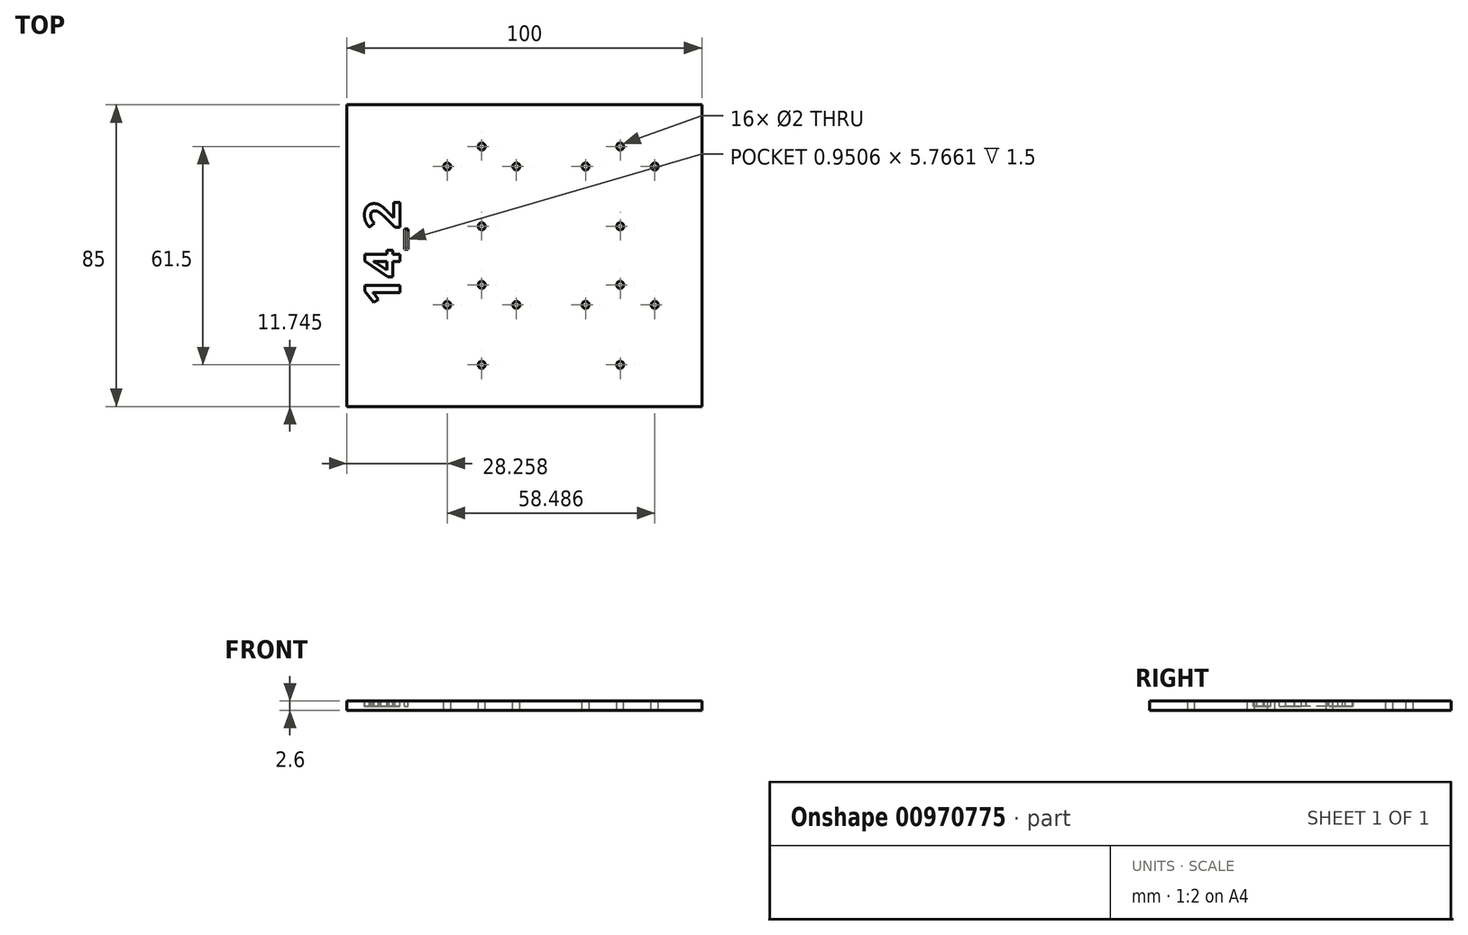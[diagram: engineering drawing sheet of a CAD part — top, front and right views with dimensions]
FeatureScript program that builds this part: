
annotation { "Feature Type Name" : "Feature", "Feature Type Description" : "" }
export const myFeature = defineFeature(function(context is Context, id is Id, definition is map)
    precondition{}
    {
        {
            var Q0;
            Q0=qCreatedBy(makeId("Top.planeOp"),FACE);
            var sketch = newSketch(context, id + "F0", { "sketchPlane" : qUnion([Q0])});
            skLineSegment(sketch, "E0.bottom", {"start": v(-43.16, 63.34) * mm, "end": v(56.84, 63.34) * mm});
            skLineSegment(sketch, "E0.top", {"start": v(-43.16, -21.66) * mm, "end": v(56.84, -21.66) * mm});
            skLineSegment(sketch, "E0.left", {"start": v(-43.16, 63.34) * mm, "end": v(-43.16, -21.66) * mm});
            skLineSegment(sketch, "E0.right", {"start": v(56.84, 63.34) * mm, "end": v(56.84, -21.66) * mm});
            skSolve(sketch);
        }
        {
            var Q0;
            Q0=makeQuery(id+"F0.imprint","IMPRINT",FACE,{"disambiguationData":[TD([[makeQuery(id+"F0.imprint","IMPRINT",EDGE,{"derivedFrom":sQuery(id+"F0.wireOp",EDGE,"E0.bottom")}),-1.0]])]});
            extrude(context, id + "F1", {"entities" : qUnion([Q0]), "depth" : 2.6 * mm, "offsetDistance" : 25 * mm});
        }
        {
            var Q0;
            Q0=makeQuery(id+"F1.opExtrude","CAP_FACE",FACE,{"disambiguationData":[OSD([sQuery(id+"F0.wireOp",EDGE,"E0.bottom"),sQuery(id+"F0.wireOp",EDGE,"E0.top"),sQuery(id+"F0.wireOp",EDGE,"E0.left"),sQuery(id+"F0.wireOp",EDGE,"E0.right")])],"isStart":false});
            var sketch = newSketch(context, id + "F2", { "sketchPlane" : qUnion([Q0])});
            skText(sketch, "E1", { "text": "14_2", "fontName": "OpenSans-Bold.ttf"});
            const initialGuessF2  = {"E1": [-0.02816, 0.00674, 0, 1, 0.01]};
            skSetInitialGuess(sketch, initialGuessF2);
            skSolve(sketch);
        }
        {
            var Q0;
            Q0=qSketchRegion(id+"F2",true);
            extrude(context, id + "F3", {"entities" : qUnion([Q0]), "operationType" : NewBodyOperationType.REMOVE, "oppositeDirection" : true, "depth" : 1.5 * mm, "offsetDistance" : 25 * mm});
        }
        {
            var Q0;
            {var subQ0=sQuery(id+"F0.wireOp",EDGE,"E0.left");var subQ1=sQuery(id+"F0.wireOp",EDGE,"E0.bottom");var subQ2=sQuery(id+"F0.wireOp",EDGE,"E0.right");var subQ3=sQuery(id+"F0.wireOp",EDGE,"E0.top");Q0=makeQuery(id+"F3.boolean.opBoolean","SPLIT",FACE,{"disambiguationData":[TD([makeQuery(id+"F1.opExtrude","SWEPT_FACE",FACE,{"disambiguationData":[OSD([subQ1])]})])],"derivedFrom":makeQuery(id+"F1.opExtrude","CAP_FACE",FACE,{"disambiguationData":[OSD([subQ1,subQ3,subQ0,subQ2])],"isStart":false})});}
            var sketch = newSketch(context, id + "F4", { "sketchPlane" : qUnion([Q0])});
            skCircle(sketch, "E2", {"center": v(-5.16, 40.34) * mm, "radius": 18 * mm});
            skCircle(sketch, "E3", {"center": v(-5.16, 40.34) * mm, "radius": 11.25 * mm});
            skLineSegment(sketch, "E4", {"start": v(-5.16, 59.97) * mm, "end": v(-5.16, 16.91) * mm});
            skLineSegment(sketch, "E5", {"start": v(-5.16, 40.34) * mm, "end": v(-24.96, 51.77) * mm});
            skLineSegment(sketch, "E6", {"start": v(-5.16, 40.34) * mm, "end": v(11.93, 50.2) * mm});
            skCircle(sketch, "E7", {"center": v(-14.9, 45.96) * mm, "radius": 1 * mm});
            skCircle(sketch, "E8", {"center": v(-5.16, 51.59) * mm, "radius": 1 * mm});
            skCircle(sketch, "E9", {"center": v(4.58, 45.96) * mm, "radius": 1 * mm});
            skCircle(sketch, "E10", {"center": v(-5.16, 29.09) * mm, "radius": 1 * mm});
            skCircle(sketch, "E11", {"center": v(-5.16, 1.34) * mm, "radius": 18 * mm});
            skCircle(sketch, "E12", {"center": v(-5.16, 1.34) * mm, "radius": 11.25 * mm});
            skLineSegment(sketch, "E13", {"start": v(-5.16, 22.58) * mm, "end": v(-5.16, -20.48) * mm});
            skLineSegment(sketch, "E14", {"start": v(-5.16, 1.34) * mm, "end": v(-24.96, 12.77) * mm});
            skLineSegment(sketch, "E15", {"start": v(-5.16, 1.34) * mm, "end": v(11.93, 11.2) * mm});
            skCircle(sketch, "E16", {"center": v(-14.9, 6.96) * mm, "radius": 1 * mm});
            skCircle(sketch, "E17", {"center": v(-5.16, 12.59) * mm, "radius": 1 * mm});
            skCircle(sketch, "E18", {"center": v(4.58, 6.96) * mm, "radius": 1 * mm});
            skCircle(sketch, "E19", {"center": v(-5.16, -9.91) * mm, "radius": 1 * mm});
            skCircle(sketch, "E20", {"center": v(33.84, 40.34) * mm, "radius": 18 * mm});
            skCircle(sketch, "E21", {"center": v(33.84, 40.34) * mm, "radius": 11.25 * mm});
            skLineSegment(sketch, "E22", {"start": v(33.84, 63.65) * mm, "end": v(33.84, 20.6) * mm});
            skLineSegment(sketch, "E23", {"start": v(33.84, 40.34) * mm, "end": v(14.04, 51.77) * mm});
            skLineSegment(sketch, "E24", {"start": v(33.84, 40.34) * mm, "end": v(50.93, 50.2) * mm});
            skCircle(sketch, "E25", {"center": v(24.1, 45.96) * mm, "radius": 1 * mm});
            skCircle(sketch, "E26", {"center": v(33.84, 51.59) * mm, "radius": 1 * mm});
            skCircle(sketch, "E27", {"center": v(43.58, 45.96) * mm, "radius": 1 * mm});
            skCircle(sketch, "E28", {"center": v(33.84, 29.09) * mm, "radius": 1 * mm});
            skCircle(sketch, "E29", {"center": v(33.84, 1.34) * mm, "radius": 18 * mm});
            skCircle(sketch, "E30", {"center": v(33.84, 1.34) * mm, "radius": 11.25 * mm});
            skLineSegment(sketch, "E31", {"start": v(33.84, 25.73) * mm, "end": v(33.84, -17.33) * mm});
            skLineSegment(sketch, "E32", {"start": v(33.84, 1.34) * mm, "end": v(14.04, 12.77) * mm});
            skLineSegment(sketch, "E33", {"start": v(33.84, 1.34) * mm, "end": v(50.93, 11.2) * mm});
            skCircle(sketch, "E34", {"center": v(24.1, 6.96) * mm, "radius": 1 * mm});
            skCircle(sketch, "E35", {"center": v(33.84, 12.59) * mm, "radius": 1 * mm});
            skCircle(sketch, "E36", {"center": v(43.58, 6.96) * mm, "radius": 1 * mm});
            skCircle(sketch, "E37", {"center": v(33.84, -9.91) * mm, "radius": 1 * mm});
            skSolve(sketch);
        }
        {
            var Q0;
            {var subQ0=sQuery(id+"F4.wireOp",EDGE,"E7");var subQ1=sQuery(id+"F4.wireOp",EDGE,"E3");var subQ2=makeQuery(id+"F4.imprint","INTERSECT",VERTEX,{"disambiguationData":[OD(0.0)],"derivedFrom":[subQ1,subQ0]});Q0=makeQuery(id+"F4.imprint","IMPRINT",FACE,{"disambiguationData":[TD([[makeQuery(id+"F4.imprint","IMPRINT",EDGE,{"disambiguationData":[TD([[subQ2,-1.0]])],"derivedFrom":subQ1}),-1.0]])]});}
            var Q1;
            {var subQ0=sQuery(id+"F4.wireOp",EDGE,"E7");var subQ1=sQuery(id+"F4.wireOp",EDGE,"E3");var subQ2=makeQuery(id+"F4.imprint","INTERSECT",VERTEX,{"disambiguationData":[OD(0.0)],"derivedFrom":[subQ1,subQ0]});Q1=makeQuery(id+"F4.imprint","IMPRINT",FACE,{"disambiguationData":[TD([[makeQuery(id+"F4.imprint","IMPRINT",EDGE,{"disambiguationData":[TD([[subQ2,-1.0]])],"derivedFrom":subQ1}),1.0]])]});}
            var Q2;
            {var subQ0=sQuery(id+"F4.wireOp",EDGE,"E5");var subQ1=sQuery(id+"F4.wireOp",EDGE,"E3");var subQ2=makeQuery(id+"F4.imprint","INTERSECT",VERTEX,{"derivedFrom":[subQ1,subQ0]});Q2=makeQuery(id+"F4.imprint","IMPRINT",FACE,{"disambiguationData":[TD([[makeQuery(id+"F4.imprint","IMPRINT",EDGE,{"disambiguationData":[TD([[subQ2,-1.0]])],"derivedFrom":subQ1}),1.0]])]});}
            var Q3;
            {var subQ0=sQuery(id+"F4.wireOp",EDGE,"E5");var subQ1=sQuery(id+"F4.wireOp",EDGE,"E3");var subQ2=makeQuery(id+"F4.imprint","INTERSECT",VERTEX,{"derivedFrom":[subQ1,subQ0]});Q3=makeQuery(id+"F4.imprint","IMPRINT",FACE,{"disambiguationData":[TD([[makeQuery(id+"F4.imprint","IMPRINT",EDGE,{"disambiguationData":[TD([[subQ2,-1.0]])],"derivedFrom":subQ1}),-1.0]])]});}
            var Q4;
            {var subQ0=sQuery(id+"F4.wireOp",EDGE,"E4");var subQ1=sQuery(id+"F4.wireOp",EDGE,"E3");var subQ2=makeQuery(id+"F4.imprint","INTERSECT",VERTEX,{"disambiguationData":[OD(0.0)],"derivedFrom":[subQ1,subQ0]});Q4=makeQuery(id+"F4.imprint","IMPRINT",FACE,{"disambiguationData":[TD([[makeQuery(id+"F4.imprint","IMPRINT",EDGE,{"disambiguationData":[TD([[subQ2,-1.0]])],"derivedFrom":subQ1}),-1.0]])]});}
            var Q5;
            {var subQ0=sQuery(id+"F4.wireOp",EDGE,"E8");var subQ1=sQuery(id+"F4.wireOp",EDGE,"E3");var subQ2=makeQuery(id+"F4.imprint","INTERSECT",VERTEX,{"disambiguationData":[OD(0.0)],"derivedFrom":[subQ1,subQ0]});Q5=makeQuery(id+"F4.imprint","IMPRINT",FACE,{"disambiguationData":[TD([[makeQuery(id+"F4.imprint","IMPRINT",EDGE,{"disambiguationData":[TD([[subQ2,-1.0]])],"derivedFrom":subQ1}),-1.0]])]});}
            var Q6;
            {var subQ0=sQuery(id+"F4.wireOp",EDGE,"E8");var subQ1=sQuery(id+"F4.wireOp",EDGE,"E3");var subQ2=makeQuery(id+"F4.imprint","INTERSECT",VERTEX,{"disambiguationData":[OD(0.0)],"derivedFrom":[subQ1,subQ0]});Q6=makeQuery(id+"F4.imprint","IMPRINT",FACE,{"disambiguationData":[TD([[makeQuery(id+"F4.imprint","IMPRINT",EDGE,{"disambiguationData":[TD([[subQ2,-1.0]])],"derivedFrom":subQ1}),1.0]])]});}
            var Q7;
            {var subQ0=sQuery(id+"F4.wireOp",EDGE,"E4");var subQ1=sQuery(id+"F4.wireOp",EDGE,"E3");var subQ2=makeQuery(id+"F4.imprint","INTERSECT",VERTEX,{"disambiguationData":[OD(0.0)],"derivedFrom":[subQ1,subQ0]});Q7=makeQuery(id+"F4.imprint","IMPRINT",FACE,{"disambiguationData":[TD([[makeQuery(id+"F4.imprint","IMPRINT",EDGE,{"disambiguationData":[TD([[subQ2,-1.0]])],"derivedFrom":subQ1}),1.0]])]});}
            var Q8;
            {var subQ0=sQuery(id+"F4.wireOp",EDGE,"E6");var subQ1=sQuery(id+"F4.wireOp",EDGE,"E3");var subQ2=makeQuery(id+"F4.imprint","INTERSECT",VERTEX,{"derivedFrom":[subQ1,subQ0]});Q8=makeQuery(id+"F4.imprint","IMPRINT",FACE,{"disambiguationData":[TD([[makeQuery(id+"F4.imprint","IMPRINT",EDGE,{"disambiguationData":[TD([[subQ2,1.0]])],"derivedFrom":subQ1}),-1.0]])]});}
            var Q9;
            {var subQ0=sQuery(id+"F4.wireOp",EDGE,"E6");var subQ1=sQuery(id+"F4.wireOp",EDGE,"E3");var subQ2=makeQuery(id+"F4.imprint","INTERSECT",VERTEX,{"derivedFrom":[subQ1,subQ0]});Q9=makeQuery(id+"F4.imprint","IMPRINT",FACE,{"disambiguationData":[TD([[makeQuery(id+"F4.imprint","IMPRINT",EDGE,{"disambiguationData":[TD([[subQ2,-1.0]])],"derivedFrom":subQ1}),1.0]])]});}
            var Q10;
            {var subQ0=sQuery(id+"F4.wireOp",EDGE,"E6");var subQ1=sQuery(id+"F4.wireOp",EDGE,"E3");var subQ2=makeQuery(id+"F4.imprint","INTERSECT",VERTEX,{"derivedFrom":[subQ1,subQ0]});Q10=makeQuery(id+"F4.imprint","IMPRINT",FACE,{"disambiguationData":[TD([[makeQuery(id+"F4.imprint","IMPRINT",EDGE,{"disambiguationData":[TD([[subQ2,-1.0]])],"derivedFrom":subQ1}),-1.0]])]});}
            var Q11;
            {var subQ0=sQuery(id+"F4.wireOp",EDGE,"E6");var subQ1=sQuery(id+"F4.wireOp",EDGE,"E3");var subQ2=makeQuery(id+"F4.imprint","INTERSECT",VERTEX,{"derivedFrom":[subQ1,subQ0]});Q11=makeQuery(id+"F4.imprint","IMPRINT",FACE,{"disambiguationData":[TD([[makeQuery(id+"F4.imprint","IMPRINT",EDGE,{"disambiguationData":[TD([[subQ2,1.0]])],"derivedFrom":subQ1}),1.0]])]});}
            var Q12;
            {var subQ0=sQuery(id+"F4.wireOp",EDGE,"E23");var subQ1=sQuery(id+"F4.wireOp",EDGE,"E21");var subQ2=makeQuery(id+"F4.imprint","INTERSECT",VERTEX,{"derivedFrom":[subQ1,subQ0]});Q12=makeQuery(id+"F4.imprint","IMPRINT",FACE,{"disambiguationData":[TD([[makeQuery(id+"F4.imprint","IMPRINT",EDGE,{"disambiguationData":[TD([[subQ2,-1.0]])],"derivedFrom":subQ1}),-1.0]])]});}
            var Q13;
            {var subQ0=sQuery(id+"F4.wireOp",EDGE,"E23");var subQ1=sQuery(id+"F4.wireOp",EDGE,"E21");var subQ2=makeQuery(id+"F4.imprint","INTERSECT",VERTEX,{"derivedFrom":[subQ1,subQ0]});Q13=makeQuery(id+"F4.imprint","IMPRINT",FACE,{"disambiguationData":[TD([[makeQuery(id+"F4.imprint","IMPRINT",EDGE,{"disambiguationData":[TD([[subQ2,-1.0]])],"derivedFrom":subQ1}),1.0]])]});}
            var Q14;
            {var subQ0=sQuery(id+"F4.wireOp",EDGE,"E25");var subQ1=sQuery(id+"F4.wireOp",EDGE,"E21");var subQ2=makeQuery(id+"F4.imprint","INTERSECT",VERTEX,{"disambiguationData":[OD(0.0)],"derivedFrom":[subQ1,subQ0]});Q14=makeQuery(id+"F4.imprint","IMPRINT",FACE,{"disambiguationData":[TD([[makeQuery(id+"F4.imprint","IMPRINT",EDGE,{"disambiguationData":[TD([[subQ2,-1.0]])],"derivedFrom":subQ1}),-1.0]])]});}
            var Q15;
            {var subQ0=sQuery(id+"F4.wireOp",EDGE,"E25");var subQ1=sQuery(id+"F4.wireOp",EDGE,"E21");var subQ2=makeQuery(id+"F4.imprint","INTERSECT",VERTEX,{"disambiguationData":[OD(0.0)],"derivedFrom":[subQ1,subQ0]});Q15=makeQuery(id+"F4.imprint","IMPRINT",FACE,{"disambiguationData":[TD([[makeQuery(id+"F4.imprint","IMPRINT",EDGE,{"disambiguationData":[TD([[subQ2,-1.0]])],"derivedFrom":subQ1}),1.0]])]});}
            var Q16;
            {var subQ0=sQuery(id+"F4.wireOp",EDGE,"E26");var subQ1=sQuery(id+"F4.wireOp",EDGE,"E21");var subQ2=makeQuery(id+"F4.imprint","INTERSECT",VERTEX,{"disambiguationData":[OD(0.0)],"derivedFrom":[subQ1,subQ0]});Q16=makeQuery(id+"F4.imprint","IMPRINT",FACE,{"disambiguationData":[TD([[makeQuery(id+"F4.imprint","IMPRINT",EDGE,{"disambiguationData":[TD([[subQ2,-1.0]])],"derivedFrom":subQ1}),1.0]])]});}
            var Q17;
            {var subQ0=sQuery(id+"F4.wireOp",EDGE,"E26");var subQ1=sQuery(id+"F4.wireOp",EDGE,"E21");var subQ2=makeQuery(id+"F4.imprint","INTERSECT",VERTEX,{"disambiguationData":[OD(0.0)],"derivedFrom":[subQ1,subQ0]});Q17=makeQuery(id+"F4.imprint","IMPRINT",FACE,{"disambiguationData":[TD([[makeQuery(id+"F4.imprint","IMPRINT",EDGE,{"disambiguationData":[TD([[subQ2,-1.0]])],"derivedFrom":subQ1}),-1.0]])]});}
            var Q18;
            {var subQ0=sQuery(id+"F4.wireOp",EDGE,"E22");var subQ1=sQuery(id+"F4.wireOp",EDGE,"E21");var subQ2=makeQuery(id+"F4.imprint","INTERSECT",VERTEX,{"disambiguationData":[OD(0.0)],"derivedFrom":[subQ1,subQ0]});Q18=makeQuery(id+"F4.imprint","IMPRINT",FACE,{"disambiguationData":[TD([[makeQuery(id+"F4.imprint","IMPRINT",EDGE,{"disambiguationData":[TD([[subQ2,-1.0]])],"derivedFrom":subQ1}),1.0]])]});}
            var Q19;
            {var subQ0=sQuery(id+"F4.wireOp",EDGE,"E22");var subQ1=sQuery(id+"F4.wireOp",EDGE,"E21");var subQ2=makeQuery(id+"F4.imprint","INTERSECT",VERTEX,{"disambiguationData":[OD(0.0)],"derivedFrom":[subQ1,subQ0]});Q19=makeQuery(id+"F4.imprint","IMPRINT",FACE,{"disambiguationData":[TD([[makeQuery(id+"F4.imprint","IMPRINT",EDGE,{"disambiguationData":[TD([[subQ2,-1.0]])],"derivedFrom":subQ1}),-1.0]])]});}
            var Q20;
            {var subQ0=sQuery(id+"F4.wireOp",EDGE,"E24");var subQ1=sQuery(id+"F4.wireOp",EDGE,"E21");var subQ2=makeQuery(id+"F4.imprint","INTERSECT",VERTEX,{"derivedFrom":[subQ1,subQ0]});Q20=makeQuery(id+"F4.imprint","IMPRINT",FACE,{"disambiguationData":[TD([[makeQuery(id+"F4.imprint","IMPRINT",EDGE,{"disambiguationData":[TD([[subQ2,1.0]])],"derivedFrom":subQ1}),1.0]])]});}
            var Q21;
            {var subQ0=sQuery(id+"F4.wireOp",EDGE,"E24");var subQ1=sQuery(id+"F4.wireOp",EDGE,"E21");var subQ2=makeQuery(id+"F4.imprint","INTERSECT",VERTEX,{"derivedFrom":[subQ1,subQ0]});Q21=makeQuery(id+"F4.imprint","IMPRINT",FACE,{"disambiguationData":[TD([[makeQuery(id+"F4.imprint","IMPRINT",EDGE,{"disambiguationData":[TD([[subQ2,-1.0]])],"derivedFrom":subQ1}),-1.0]])]});}
            var Q22;
            {var subQ0=sQuery(id+"F4.wireOp",EDGE,"E24");var subQ1=sQuery(id+"F4.wireOp",EDGE,"E21");var subQ2=makeQuery(id+"F4.imprint","INTERSECT",VERTEX,{"derivedFrom":[subQ1,subQ0]});Q22=makeQuery(id+"F4.imprint","IMPRINT",FACE,{"disambiguationData":[TD([[makeQuery(id+"F4.imprint","IMPRINT",EDGE,{"disambiguationData":[TD([[subQ2,1.0]])],"derivedFrom":subQ1}),-1.0]])]});}
            var Q23;
            {var subQ0=sQuery(id+"F4.wireOp",EDGE,"E24");var subQ1=sQuery(id+"F4.wireOp",EDGE,"E21");var subQ2=makeQuery(id+"F4.imprint","INTERSECT",VERTEX,{"derivedFrom":[subQ1,subQ0]});Q23=makeQuery(id+"F4.imprint","IMPRINT",FACE,{"disambiguationData":[TD([[makeQuery(id+"F4.imprint","IMPRINT",EDGE,{"disambiguationData":[TD([[subQ2,-1.0]])],"derivedFrom":subQ1}),1.0]])]});}
            var Q24;
            {var subQ0=sQuery(id+"F4.wireOp",EDGE,"E10");var subQ1=sQuery(id+"F4.wireOp",EDGE,"E3");var subQ2=makeQuery(id+"F4.imprint","INTERSECT",VERTEX,{"disambiguationData":[OD(0.0)],"derivedFrom":[subQ1,subQ0]});Q24=makeQuery(id+"F4.imprint","IMPRINT",FACE,{"disambiguationData":[TD([[makeQuery(id+"F4.imprint","IMPRINT",EDGE,{"disambiguationData":[TD([[subQ2,-1.0]])],"derivedFrom":subQ1}),1.0]])]});}
            var Q25;
            {var subQ0=sQuery(id+"F4.wireOp",EDGE,"E10");var subQ1=sQuery(id+"F4.wireOp",EDGE,"E3");var subQ2=makeQuery(id+"F4.imprint","INTERSECT",VERTEX,{"disambiguationData":[OD(0.0)],"derivedFrom":[subQ1,subQ0]});Q25=makeQuery(id+"F4.imprint","IMPRINT",FACE,{"disambiguationData":[TD([[makeQuery(id+"F4.imprint","IMPRINT",EDGE,{"disambiguationData":[TD([[subQ2,-1.0]])],"derivedFrom":subQ1}),-1.0]])]});}
            var Q26;
            {var subQ0=sQuery(id+"F4.wireOp",EDGE,"E4");var subQ1=sQuery(id+"F4.wireOp",EDGE,"E3");var subQ2=makeQuery(id+"F4.imprint","INTERSECT",VERTEX,{"disambiguationData":[OD(1.0)],"derivedFrom":[subQ1,subQ0]});Q26=makeQuery(id+"F4.imprint","IMPRINT",FACE,{"disambiguationData":[TD([[makeQuery(id+"F4.imprint","IMPRINT",EDGE,{"disambiguationData":[TD([[subQ2,-1.0]])],"derivedFrom":subQ1}),-1.0]])]});}
            var Q27;
            {var subQ0=sQuery(id+"F4.wireOp",EDGE,"E4");var subQ1=sQuery(id+"F4.wireOp",EDGE,"E3");var subQ2=makeQuery(id+"F4.imprint","INTERSECT",VERTEX,{"disambiguationData":[OD(1.0)],"derivedFrom":[subQ1,subQ0]});Q27=makeQuery(id+"F4.imprint","IMPRINT",FACE,{"disambiguationData":[TD([[makeQuery(id+"F4.imprint","IMPRINT",EDGE,{"disambiguationData":[TD([[subQ2,-1.0]])],"derivedFrom":subQ1}),1.0]])]});}
            var Q28;
            {var subQ0=sQuery(id+"F4.wireOp",EDGE,"E28");var subQ1=sQuery(id+"F4.wireOp",EDGE,"E21");var subQ2=makeQuery(id+"F4.imprint","INTERSECT",VERTEX,{"disambiguationData":[OD(0.0)],"derivedFrom":[subQ1,subQ0]});Q28=makeQuery(id+"F4.imprint","IMPRINT",FACE,{"disambiguationData":[TD([[makeQuery(id+"F4.imprint","IMPRINT",EDGE,{"disambiguationData":[TD([[subQ2,-1.0]])],"derivedFrom":subQ1}),1.0]])]});}
            var Q29;
            {var subQ0=sQuery(id+"F4.wireOp",EDGE,"E28");var subQ1=sQuery(id+"F4.wireOp",EDGE,"E21");var subQ2=makeQuery(id+"F4.imprint","INTERSECT",VERTEX,{"disambiguationData":[OD(0.0)],"derivedFrom":[subQ1,subQ0]});Q29=makeQuery(id+"F4.imprint","IMPRINT",FACE,{"disambiguationData":[TD([[makeQuery(id+"F4.imprint","IMPRINT",EDGE,{"disambiguationData":[TD([[subQ2,-1.0]])],"derivedFrom":subQ1}),-1.0]])]});}
            var Q30;
            {var subQ0=sQuery(id+"F4.wireOp",EDGE,"E22");var subQ1=sQuery(id+"F4.wireOp",EDGE,"E21");var subQ2=makeQuery(id+"F4.imprint","INTERSECT",VERTEX,{"disambiguationData":[OD(1.0)],"derivedFrom":[subQ1,subQ0]});Q30=makeQuery(id+"F4.imprint","IMPRINT",FACE,{"disambiguationData":[TD([[makeQuery(id+"F4.imprint","IMPRINT",EDGE,{"disambiguationData":[TD([[subQ2,-1.0]])],"derivedFrom":subQ1}),-1.0]])]});}
            var Q31;
            {var subQ0=sQuery(id+"F4.wireOp",EDGE,"E22");var subQ1=sQuery(id+"F4.wireOp",EDGE,"E21");var subQ2=makeQuery(id+"F4.imprint","INTERSECT",VERTEX,{"disambiguationData":[OD(1.0)],"derivedFrom":[subQ1,subQ0]});Q31=makeQuery(id+"F4.imprint","IMPRINT",FACE,{"disambiguationData":[TD([[makeQuery(id+"F4.imprint","IMPRINT",EDGE,{"disambiguationData":[TD([[subQ2,-1.0]])],"derivedFrom":subQ1}),1.0]])]});}
            var Q32;
            {var subQ0=sQuery(id+"F4.wireOp",EDGE,"E14");var subQ1=sQuery(id+"F4.wireOp",EDGE,"E12");var subQ2=makeQuery(id+"F4.imprint","INTERSECT",VERTEX,{"derivedFrom":[subQ1,subQ0]});Q32=makeQuery(id+"F4.imprint","IMPRINT",FACE,{"disambiguationData":[TD([[makeQuery(id+"F4.imprint","IMPRINT",EDGE,{"disambiguationData":[TD([[subQ2,-1.0]])],"derivedFrom":subQ1}),1.0]])]});}
            var Q33;
            {var subQ0=sQuery(id+"F4.wireOp",EDGE,"E16");var subQ1=sQuery(id+"F4.wireOp",EDGE,"E12");var subQ2=makeQuery(id+"F4.imprint","INTERSECT",VERTEX,{"disambiguationData":[OD(0.0)],"derivedFrom":[subQ1,subQ0]});Q33=makeQuery(id+"F4.imprint","IMPRINT",FACE,{"disambiguationData":[TD([[makeQuery(id+"F4.imprint","IMPRINT",EDGE,{"disambiguationData":[TD([[subQ2,-1.0]])],"derivedFrom":subQ1}),1.0]])]});}
            var Q34;
            {var subQ0=sQuery(id+"F4.wireOp",EDGE,"E14");var subQ1=sQuery(id+"F4.wireOp",EDGE,"E12");var subQ2=makeQuery(id+"F4.imprint","INTERSECT",VERTEX,{"derivedFrom":[subQ1,subQ0]});Q34=makeQuery(id+"F4.imprint","IMPRINT",FACE,{"disambiguationData":[TD([[makeQuery(id+"F4.imprint","IMPRINT",EDGE,{"disambiguationData":[TD([[subQ2,-1.0]])],"derivedFrom":subQ1}),-1.0]])]});}
            var Q35;
            {var subQ0=sQuery(id+"F4.wireOp",EDGE,"E16");var subQ1=sQuery(id+"F4.wireOp",EDGE,"E12");var subQ2=makeQuery(id+"F4.imprint","INTERSECT",VERTEX,{"disambiguationData":[OD(0.0)],"derivedFrom":[subQ1,subQ0]});Q35=makeQuery(id+"F4.imprint","IMPRINT",FACE,{"disambiguationData":[TD([[makeQuery(id+"F4.imprint","IMPRINT",EDGE,{"disambiguationData":[TD([[subQ2,-1.0]])],"derivedFrom":subQ1}),-1.0]])]});}
            var Q36;
            {var subQ0=sQuery(id+"F4.wireOp",EDGE,"E15");var subQ1=sQuery(id+"F4.wireOp",EDGE,"E12");var subQ2=makeQuery(id+"F4.imprint","INTERSECT",VERTEX,{"derivedFrom":[subQ1,subQ0]});Q36=makeQuery(id+"F4.imprint","IMPRINT",FACE,{"disambiguationData":[TD([[makeQuery(id+"F4.imprint","IMPRINT",EDGE,{"disambiguationData":[TD([[subQ2,1.0]])],"derivedFrom":subQ1}),-1.0]])]});}
            var Q37;
            {var subQ0=sQuery(id+"F4.wireOp",EDGE,"E15");var subQ1=sQuery(id+"F4.wireOp",EDGE,"E12");var subQ2=makeQuery(id+"F4.imprint","INTERSECT",VERTEX,{"derivedFrom":[subQ1,subQ0]});Q37=makeQuery(id+"F4.imprint","IMPRINT",FACE,{"disambiguationData":[TD([[makeQuery(id+"F4.imprint","IMPRINT",EDGE,{"disambiguationData":[TD([[subQ2,-1.0]])],"derivedFrom":subQ1}),-1.0]])]});}
            var Q38;
            {var subQ0=sQuery(id+"F4.wireOp",EDGE,"E15");var subQ1=sQuery(id+"F4.wireOp",EDGE,"E12");var subQ2=makeQuery(id+"F4.imprint","INTERSECT",VERTEX,{"derivedFrom":[subQ1,subQ0]});Q38=makeQuery(id+"F4.imprint","IMPRINT",FACE,{"disambiguationData":[TD([[makeQuery(id+"F4.imprint","IMPRINT",EDGE,{"disambiguationData":[TD([[subQ2,-1.0]])],"derivedFrom":subQ1}),1.0]])]});}
            var Q39;
            {var subQ0=sQuery(id+"F4.wireOp",EDGE,"E15");var subQ1=sQuery(id+"F4.wireOp",EDGE,"E12");var subQ2=makeQuery(id+"F4.imprint","INTERSECT",VERTEX,{"derivedFrom":[subQ1,subQ0]});Q39=makeQuery(id+"F4.imprint","IMPRINT",FACE,{"disambiguationData":[TD([[makeQuery(id+"F4.imprint","IMPRINT",EDGE,{"disambiguationData":[TD([[subQ2,1.0]])],"derivedFrom":subQ1}),1.0]])]});}
            var Q40;
            {var subQ0=sQuery(id+"F4.wireOp",EDGE,"E17");var subQ1=sQuery(id+"F4.wireOp",EDGE,"E12");var subQ2=makeQuery(id+"F4.imprint","INTERSECT",VERTEX,{"disambiguationData":[OD(0.0)],"derivedFrom":[subQ1,subQ0]});Q40=makeQuery(id+"F4.imprint","IMPRINT",FACE,{"disambiguationData":[TD([[makeQuery(id+"F4.imprint","IMPRINT",EDGE,{"disambiguationData":[TD([[subQ2,-1.0]])],"derivedFrom":subQ1}),1.0]])]});}
            var Q41;
            {var subQ0=sQuery(id+"F4.wireOp",EDGE,"E13");var subQ1=sQuery(id+"F4.wireOp",EDGE,"E12");var subQ2=makeQuery(id+"F4.imprint","INTERSECT",VERTEX,{"disambiguationData":[OD(0.0)],"derivedFrom":[subQ1,subQ0]});Q41=makeQuery(id+"F4.imprint","IMPRINT",FACE,{"disambiguationData":[TD([[makeQuery(id+"F4.imprint","IMPRINT",EDGE,{"disambiguationData":[TD([[subQ2,-1.0]])],"derivedFrom":subQ1}),1.0]])]});}
            var Q42;
            {var subQ0=sQuery(id+"F4.wireOp",EDGE,"E17");var subQ1=sQuery(id+"F4.wireOp",EDGE,"E12");var subQ2=makeQuery(id+"F4.imprint","INTERSECT",VERTEX,{"disambiguationData":[OD(0.0)],"derivedFrom":[subQ1,subQ0]});Q42=makeQuery(id+"F4.imprint","IMPRINT",FACE,{"disambiguationData":[TD([[makeQuery(id+"F4.imprint","IMPRINT",EDGE,{"disambiguationData":[TD([[subQ2,-1.0]])],"derivedFrom":subQ1}),-1.0]])]});}
            var Q43;
            {var subQ0=sQuery(id+"F4.wireOp",EDGE,"E13");var subQ1=sQuery(id+"F4.wireOp",EDGE,"E12");var subQ2=makeQuery(id+"F4.imprint","INTERSECT",VERTEX,{"disambiguationData":[OD(0.0)],"derivedFrom":[subQ1,subQ0]});Q43=makeQuery(id+"F4.imprint","IMPRINT",FACE,{"disambiguationData":[TD([[makeQuery(id+"F4.imprint","IMPRINT",EDGE,{"disambiguationData":[TD([[subQ2,-1.0]])],"derivedFrom":subQ1}),-1.0]])]});}
            var Q44;
            {var subQ0=sQuery(id+"F4.wireOp",EDGE,"E34");var subQ1=sQuery(id+"F4.wireOp",EDGE,"E30");var subQ2=makeQuery(id+"F4.imprint","INTERSECT",VERTEX,{"disambiguationData":[OD(0.0)],"derivedFrom":[subQ1,subQ0]});Q44=makeQuery(id+"F4.imprint","IMPRINT",FACE,{"disambiguationData":[TD([[makeQuery(id+"F4.imprint","IMPRINT",EDGE,{"disambiguationData":[TD([[subQ2,-1.0]])],"derivedFrom":subQ1}),-1.0]])]});}
            var Q45;
            {var subQ0=sQuery(id+"F4.wireOp",EDGE,"E34");var subQ1=sQuery(id+"F4.wireOp",EDGE,"E30");var subQ2=makeQuery(id+"F4.imprint","INTERSECT",VERTEX,{"disambiguationData":[OD(0.0)],"derivedFrom":[subQ1,subQ0]});Q45=makeQuery(id+"F4.imprint","IMPRINT",FACE,{"disambiguationData":[TD([[makeQuery(id+"F4.imprint","IMPRINT",EDGE,{"disambiguationData":[TD([[subQ2,-1.0]])],"derivedFrom":subQ1}),1.0]])]});}
            var Q46;
            {var subQ0=sQuery(id+"F4.wireOp",EDGE,"E33");var subQ1=sQuery(id+"F4.wireOp",EDGE,"E30");var subQ2=makeQuery(id+"F4.imprint","INTERSECT",VERTEX,{"derivedFrom":[subQ1,subQ0]});Q46=makeQuery(id+"F4.imprint","IMPRINT",FACE,{"disambiguationData":[TD([[makeQuery(id+"F4.imprint","IMPRINT",EDGE,{"disambiguationData":[TD([[subQ2,-1.0]])],"derivedFrom":subQ1}),-1.0]])]});}
            var Q47;
            {var subQ0=sQuery(id+"F4.wireOp",EDGE,"E33");var subQ1=sQuery(id+"F4.wireOp",EDGE,"E30");var subQ2=makeQuery(id+"F4.imprint","INTERSECT",VERTEX,{"derivedFrom":[subQ1,subQ0]});Q47=makeQuery(id+"F4.imprint","IMPRINT",FACE,{"disambiguationData":[TD([[makeQuery(id+"F4.imprint","IMPRINT",EDGE,{"disambiguationData":[TD([[subQ2,1.0]])],"derivedFrom":subQ1}),-1.0]])]});}
            var Q48;
            {var subQ0=sQuery(id+"F4.wireOp",EDGE,"E33");var subQ1=sQuery(id+"F4.wireOp",EDGE,"E30");var subQ2=makeQuery(id+"F4.imprint","INTERSECT",VERTEX,{"derivedFrom":[subQ1,subQ0]});Q48=makeQuery(id+"F4.imprint","IMPRINT",FACE,{"disambiguationData":[TD([[makeQuery(id+"F4.imprint","IMPRINT",EDGE,{"disambiguationData":[TD([[subQ2,1.0]])],"derivedFrom":subQ1}),1.0]])]});}
            var Q49;
            {var subQ0=sQuery(id+"F4.wireOp",EDGE,"E32");var subQ1=sQuery(id+"F4.wireOp",EDGE,"E30");var subQ2=makeQuery(id+"F4.imprint","INTERSECT",VERTEX,{"derivedFrom":[subQ1,subQ0]});Q49=makeQuery(id+"F4.imprint","IMPRINT",FACE,{"disambiguationData":[TD([[makeQuery(id+"F4.imprint","IMPRINT",EDGE,{"disambiguationData":[TD([[subQ2,-1.0]])],"derivedFrom":subQ1}),1.0]])]});}
            var Q50;
            {var subQ0=sQuery(id+"F4.wireOp",EDGE,"E32");var subQ1=sQuery(id+"F4.wireOp",EDGE,"E30");var subQ2=makeQuery(id+"F4.imprint","INTERSECT",VERTEX,{"derivedFrom":[subQ1,subQ0]});Q50=makeQuery(id+"F4.imprint","IMPRINT",FACE,{"disambiguationData":[TD([[makeQuery(id+"F4.imprint","IMPRINT",EDGE,{"disambiguationData":[TD([[subQ2,-1.0]])],"derivedFrom":subQ1}),-1.0]])]});}
            var Q51;
            {var subQ0=sQuery(id+"F4.wireOp",EDGE,"E33");var subQ1=sQuery(id+"F4.wireOp",EDGE,"E30");var subQ2=makeQuery(id+"F4.imprint","INTERSECT",VERTEX,{"derivedFrom":[subQ1,subQ0]});Q51=makeQuery(id+"F4.imprint","IMPRINT",FACE,{"disambiguationData":[TD([[makeQuery(id+"F4.imprint","IMPRINT",EDGE,{"disambiguationData":[TD([[subQ2,-1.0]])],"derivedFrom":subQ1}),1.0]])]});}
            var Q52;
            {var subQ0=sQuery(id+"F4.wireOp",EDGE,"E31");var subQ1=sQuery(id+"F4.wireOp",EDGE,"E30");var subQ2=makeQuery(id+"F4.imprint","INTERSECT",VERTEX,{"disambiguationData":[OD(0.0)],"derivedFrom":[subQ1,subQ0]});Q52=makeQuery(id+"F4.imprint","IMPRINT",FACE,{"disambiguationData":[TD([[makeQuery(id+"F4.imprint","IMPRINT",EDGE,{"disambiguationData":[TD([[subQ2,-1.0]])],"derivedFrom":subQ1}),-1.0]])]});}
            var Q53;
            {var subQ0=sQuery(id+"F4.wireOp",EDGE,"E31");var subQ1=sQuery(id+"F4.wireOp",EDGE,"E30");var subQ2=makeQuery(id+"F4.imprint","INTERSECT",VERTEX,{"disambiguationData":[OD(0.0)],"derivedFrom":[subQ1,subQ0]});Q53=makeQuery(id+"F4.imprint","IMPRINT",FACE,{"disambiguationData":[TD([[makeQuery(id+"F4.imprint","IMPRINT",EDGE,{"disambiguationData":[TD([[subQ2,-1.0]])],"derivedFrom":subQ1}),1.0]])]});}
            var Q54;
            {var subQ0=sQuery(id+"F4.wireOp",EDGE,"E35");var subQ1=sQuery(id+"F4.wireOp",EDGE,"E30");var subQ2=makeQuery(id+"F4.imprint","INTERSECT",VERTEX,{"disambiguationData":[OD(0.0)],"derivedFrom":[subQ1,subQ0]});Q54=makeQuery(id+"F4.imprint","IMPRINT",FACE,{"disambiguationData":[TD([[makeQuery(id+"F4.imprint","IMPRINT",EDGE,{"disambiguationData":[TD([[subQ2,-1.0]])],"derivedFrom":subQ1}),-1.0]])]});}
            var Q55;
            {var subQ0=sQuery(id+"F4.wireOp",EDGE,"E35");var subQ1=sQuery(id+"F4.wireOp",EDGE,"E30");var subQ2=makeQuery(id+"F4.imprint","INTERSECT",VERTEX,{"disambiguationData":[OD(0.0)],"derivedFrom":[subQ1,subQ0]});Q55=makeQuery(id+"F4.imprint","IMPRINT",FACE,{"disambiguationData":[TD([[makeQuery(id+"F4.imprint","IMPRINT",EDGE,{"disambiguationData":[TD([[subQ2,-1.0]])],"derivedFrom":subQ1}),1.0]])]});}
            var Q56;
            {var subQ0=sQuery(id+"F4.wireOp",EDGE,"E13");var subQ1=sQuery(id+"F4.wireOp",EDGE,"E12");var subQ2=makeQuery(id+"F4.imprint","INTERSECT",VERTEX,{"disambiguationData":[OD(1.0)],"derivedFrom":[subQ1,subQ0]});Q56=makeQuery(id+"F4.imprint","IMPRINT",FACE,{"disambiguationData":[TD([[makeQuery(id+"F4.imprint","IMPRINT",EDGE,{"disambiguationData":[TD([[subQ2,-1.0]])],"derivedFrom":subQ1}),-1.0]])]});}
            var Q57;
            {var subQ0=sQuery(id+"F4.wireOp",EDGE,"E13");var subQ1=sQuery(id+"F4.wireOp",EDGE,"E12");var subQ2=makeQuery(id+"F4.imprint","INTERSECT",VERTEX,{"disambiguationData":[OD(1.0)],"derivedFrom":[subQ1,subQ0]});Q57=makeQuery(id+"F4.imprint","IMPRINT",FACE,{"disambiguationData":[TD([[makeQuery(id+"F4.imprint","IMPRINT",EDGE,{"disambiguationData":[TD([[subQ2,-1.0]])],"derivedFrom":subQ1}),1.0]])]});}
            var Q58;
            {var subQ0=sQuery(id+"F4.wireOp",EDGE,"E19");var subQ1=sQuery(id+"F4.wireOp",EDGE,"E12");var subQ2=makeQuery(id+"F4.imprint","INTERSECT",VERTEX,{"disambiguationData":[OD(0.0)],"derivedFrom":[subQ1,subQ0]});Q58=makeQuery(id+"F4.imprint","IMPRINT",FACE,{"disambiguationData":[TD([[makeQuery(id+"F4.imprint","IMPRINT",EDGE,{"disambiguationData":[TD([[subQ2,-1.0]])],"derivedFrom":subQ1}),1.0]])]});}
            var Q59;
            {var subQ0=sQuery(id+"F4.wireOp",EDGE,"E19");var subQ1=sQuery(id+"F4.wireOp",EDGE,"E12");var subQ2=makeQuery(id+"F4.imprint","INTERSECT",VERTEX,{"disambiguationData":[OD(0.0)],"derivedFrom":[subQ1,subQ0]});Q59=makeQuery(id+"F4.imprint","IMPRINT",FACE,{"disambiguationData":[TD([[makeQuery(id+"F4.imprint","IMPRINT",EDGE,{"disambiguationData":[TD([[subQ2,-1.0]])],"derivedFrom":subQ1}),-1.0]])]});}
            var Q60;
            {var subQ0=sQuery(id+"F4.wireOp",EDGE,"E31");var subQ1=sQuery(id+"F4.wireOp",EDGE,"E30");var subQ2=makeQuery(id+"F4.imprint","INTERSECT",VERTEX,{"disambiguationData":[OD(1.0)],"derivedFrom":[subQ1,subQ0]});Q60=makeQuery(id+"F4.imprint","IMPRINT",FACE,{"disambiguationData":[TD([[makeQuery(id+"F4.imprint","IMPRINT",EDGE,{"disambiguationData":[TD([[subQ2,-1.0]])],"derivedFrom":subQ1}),1.0]])]});}
            var Q61;
            {var subQ0=sQuery(id+"F4.wireOp",EDGE,"E37");var subQ1=sQuery(id+"F4.wireOp",EDGE,"E30");var subQ2=makeQuery(id+"F4.imprint","INTERSECT",VERTEX,{"disambiguationData":[OD(0.0)],"derivedFrom":[subQ1,subQ0]});Q61=makeQuery(id+"F4.imprint","IMPRINT",FACE,{"disambiguationData":[TD([[makeQuery(id+"F4.imprint","IMPRINT",EDGE,{"disambiguationData":[TD([[subQ2,-1.0]])],"derivedFrom":subQ1}),-1.0]])]});}
            var Q62;
            {var subQ0=sQuery(id+"F4.wireOp",EDGE,"E37");var subQ1=sQuery(id+"F4.wireOp",EDGE,"E30");var subQ2=makeQuery(id+"F4.imprint","INTERSECT",VERTEX,{"disambiguationData":[OD(0.0)],"derivedFrom":[subQ1,subQ0]});Q62=makeQuery(id+"F4.imprint","IMPRINT",FACE,{"disambiguationData":[TD([[makeQuery(id+"F4.imprint","IMPRINT",EDGE,{"disambiguationData":[TD([[subQ2,-1.0]])],"derivedFrom":subQ1}),1.0]])]});}
            var Q63;
            {var subQ0=sQuery(id+"F4.wireOp",EDGE,"E31");var subQ1=sQuery(id+"F4.wireOp",EDGE,"E30");var subQ2=makeQuery(id+"F4.imprint","INTERSECT",VERTEX,{"disambiguationData":[OD(1.0)],"derivedFrom":[subQ1,subQ0]});Q63=makeQuery(id+"F4.imprint","IMPRINT",FACE,{"disambiguationData":[TD([[makeQuery(id+"F4.imprint","IMPRINT",EDGE,{"disambiguationData":[TD([[subQ2,-1.0]])],"derivedFrom":subQ1}),-1.0]])]});}
            extrude(context, id + "F5", {"entities" : qUnion([Q0, Q1, Q2, Q3, Q4, Q5, Q6, Q7, Q8, Q9, Q10, Q11, Q12, Q13, Q14, Q15, Q16, Q17, Q18, Q19, Q20, Q21, Q22, Q23, Q24, Q25, Q26, Q27, Q28, Q29, Q30, Q31, Q32, Q33, Q34, Q35, Q36, Q37, Q38, Q39, Q40, Q41, Q42, Q43, Q44, Q45, Q46, Q47, Q48, Q49, Q50, Q51, Q52, Q53, Q54, Q55, Q56, Q57, Q58, Q59, Q60, Q61, Q62, Q63]), "operationType" : NewBodyOperationType.REMOVE, "endBound" : BoundingType.UP_TO_NEXT, "oppositeDirection" : true, "depth" : 25 * mm, "offsetDistance" : 25 * mm});
        }
    });
